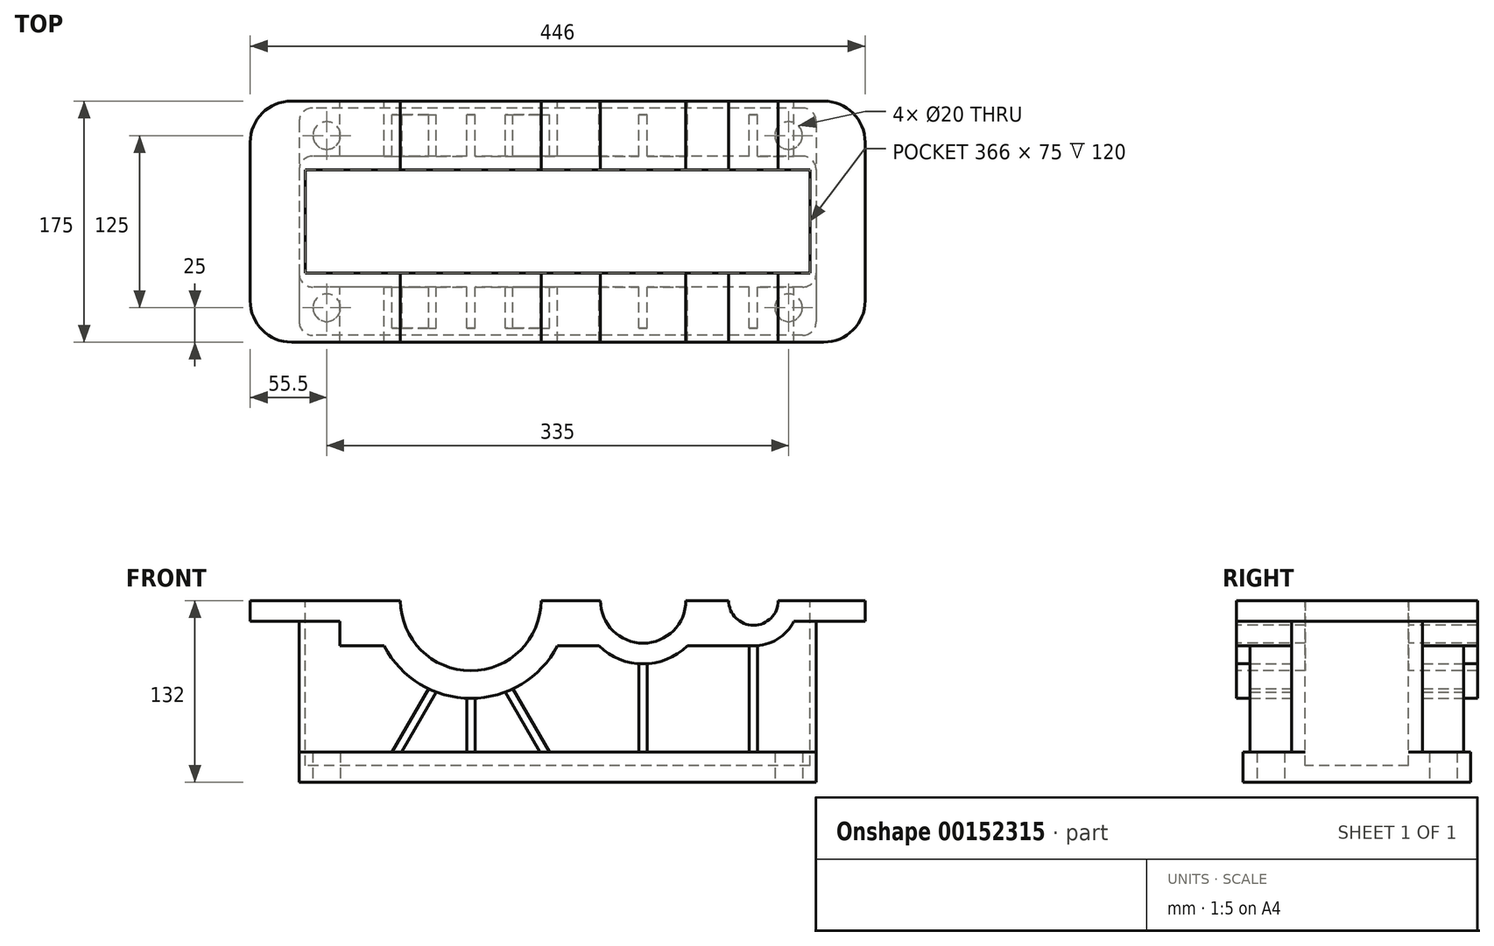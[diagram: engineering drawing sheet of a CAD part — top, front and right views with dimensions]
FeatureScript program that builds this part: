
annotation { "Feature Type Name" : "Feature", "Feature Type Description" : "" }
export const myFeature = defineFeature(function(context is Context, id is Id, definition is map)
    precondition{}
    {
        {
            var Q0;
            Q0=qCreatedBy(makeId("Top.planeOp"),FACE);
            var sketch = newSketch(context, id + "F0", { "sketchPlane" : qUnion([Q0])});
            skLineSegment(sketch, "E0.bottom", {"start": v(187.5, 82.5) * mm, "end": v(-187.5, 82.5) * mm});
            skLineSegment(sketch, "E0.top", {"start": v(187.5, -82.5) * mm, "end": v(-187.5, -82.5) * mm});
            skLineSegment(sketch, "E0.left", {"start": v(187.5, 82.5) * mm, "end": v(187.5, -82.5) * mm});
            skLineSegment(sketch, "E0.right", {"start": v(-187.5, 82.5) * mm, "end": v(-187.5, -82.5) * mm});
            skPoint(sketch, "E0.middle", {"position": v(0, 0) * mm});
            skSolve(sketch);
        }
        {
            var Q0;
            Q0 = qSketchRegion(id + "F0", true);
            extrude(context, id + "F1", {"entities" : qUnion([Q0]), "depth" : 22 * mm});
        }
        {
            var Q0;
            Q0=makeQuery(id+"F1.opExtrude","CAP_FACE",FACE,{"disambiguationData":[OSD([sQuery(id+"F0.wireOp",EDGE,"E0.bottom"),sQuery(id+"F0.wireOp",EDGE,"E0.top"),sQuery(id+"F0.wireOp",EDGE,"E0.left"),sQuery(id+"F0.wireOp",EDGE,"E0.right")])],"isStart":false});
            var sketch = newSketch(context, id + "F2", { "sketchPlane" : qUnion([Q0])});
            skLineSegment(sketch, "E1.bottom", {"start": v(187.5, 47.5) * mm, "end": v(-187.5, 47.5) * mm});
            skLineSegment(sketch, "E1.top", {"start": v(187.5, -47.5) * mm, "end": v(-187.5, -47.5) * mm});
            skLineSegment(sketch, "E1.left", {"start": v(187.5, 47.5) * mm, "end": v(187.5, -47.5) * mm});
            skLineSegment(sketch, "E1.right", {"start": v(-187.5, 47.5) * mm, "end": v(-187.5, -47.5) * mm});
            skPoint(sketch, "E1.middle", {"position": v(0, 0) * mm});
            skSolve(sketch);
        }
        {
            var Q0;
            Q0 = qSketchRegion(id + "F2", true);
            extrude(context, id + "F3", {"entities" : qUnion([Q0]), "operationType" : NewBodyOperationType.ADD, "depth" : 95 * mm});
        }
        {
            var Q0;
            Q0=makeQuery(id+"F1.opExtrude","SWEPT_EDGE",EDGE,{"disambiguationData":[OSD([sQuery(id+"F0.wireOp",EDGE,"E0.top"),sQuery(id+"F0.wireOp",EDGE,"E0.right")])]});
            var Q1;
            Q1=makeQuery(id+"F1.opExtrude","SWEPT_EDGE",EDGE,{"disambiguationData":[OSD([sQuery(id+"F0.wireOp",EDGE,"E0.top"),sQuery(id+"F0.wireOp",EDGE,"E0.left")])]});
            var Q2;
            Q2=makeQuery(id+"F1.opExtrude","SWEPT_EDGE",EDGE,{"disambiguationData":[OSD([sQuery(id+"F0.wireOp",EDGE,"E0.bottom"),sQuery(id+"F0.wireOp",EDGE,"E0.left")])]});
            var Q3;
            Q3=makeQuery(id+"F3.opExtrude","SWEPT_EDGE",EDGE,{"disambiguationData":[OSD([sQuery(id+"F0.wireOp",EDGE,"E0.left"),sQuery(id+"F2.wireOp",EDGE,"E1.bottom"),sQuery(id+"F2.wireOp",EDGE,"E1.left")])]});
            var Q4;
            Q4=makeQuery(id+"F3.opExtrude","SWEPT_EDGE",EDGE,{"disambiguationData":[OSD([sQuery(id+"F0.wireOp",EDGE,"E0.left"),sQuery(id+"F2.wireOp",EDGE,"E1.top"),sQuery(id+"F2.wireOp",EDGE,"E1.left")])]});
            var Q5;
            Q5=makeQuery(id+"F3.opExtrude","SWEPT_EDGE",EDGE,{"disambiguationData":[OSD([sQuery(id+"F0.wireOp",EDGE,"E0.right"),sQuery(id+"F2.wireOp",EDGE,"E1.top"),sQuery(id+"F2.wireOp",EDGE,"E1.right")])]});
            var Q6;
            Q6=makeQuery(id+"F3.opExtrude","SWEPT_EDGE",EDGE,{"disambiguationData":[OSD([sQuery(id+"F0.wireOp",EDGE,"E0.right"),sQuery(id+"F2.wireOp",EDGE,"E1.bottom"),sQuery(id+"F2.wireOp",EDGE,"E1.right")])]});
            var Q7;
            Q7=makeQuery(id+"F1.opExtrude","SWEPT_EDGE",EDGE,{"disambiguationData":[OSD([sQuery(id+"F0.wireOp",EDGE,"E0.bottom"),sQuery(id+"F0.wireOp",EDGE,"E0.right")])]});
            fillet(context, id + "F4", {"entities" : qUnion([Q0, Q1, Q2, Q3, Q4, Q5, Q6, Q7]), "radius" : 10 * mm, "tangentPropagation" : true, "allowEdgeOverflow" : false});
        }
        {
            var Q0;
            Q0=qCreatedBy(makeId("Front.planeOp"),FACE);
            var sketch = newSketch(context, id + "F5", { "sketchPlane" : qUnion([Q0])});
            skLineSegment(sketch, "E2", {"start": v(-223, 132) * mm, "end": v(223, 132) * mm});
            skLineSegment(sketch, "E3", {"start": v(223, 132) * mm, "end": v(223, 117) * mm});
            skLineSegment(sketch, "E4", {"start": v(223, 117) * mm, "end": v(171.4, 117) * mm});
            skLineSegment(sketch, "E5", {"start": v(-223, 132) * mm, "end": v(-223, 117) * mm});
            skLineSegment(sketch, "E6", {"start": v(-223, 117) * mm, "end": v(-157.86, 117) * mm});
            skLineSegment(sketch, "E7", {"start": v(-157.86, 117) * mm, "end": v(-157.86, 99) * mm});
            skLineSegment(sketch, "E8", {"start": v(-157.86, 99) * mm, "end": v(-125.86, 99) * mm});
            skLineSegment(sketch, "E9", {"start": v(0, 132) * mm, "end": v(0, 0) * mm, "construction": true});
            skLineSegment(sketch, "E10", {"start": v(-63, 132) * mm, "end": v(-63, 21.3) * mm, "construction": true});
            skLineSegment(sketch, "E11", {"start": v(62, 132) * mm, "end": v(62, 21.78) * mm, "construction": true});
            skLineSegment(sketch, "E12", {"start": v(142, 132) * mm, "end": v(142, 22.17) * mm, "construction": true});
            skArc(sketch, "E13", {"start": v(-125.86, 99) * mm, "mid": v(-63, 61) * mm, "end": v(-0.14, 99) * mm});
            skLineSegment(sketch, "E14", {"start": v(-0.14, 99) * mm, "end": v(29.95, 99) * mm});
            skArc(sketch, "E15", {"start": v(29.95, 99) * mm, "mid": v(62, 86) * mm, "end": v(94.05, 99) * mm});
            skLineSegment(sketch, "E16", {"start": v(94.05, 99) * mm, "end": v(142, 99) * mm});
            skArc(sketch, "E17", {"start": v(142, 99) * mm, "mid": v(159.23, 103.86) * mm, "end": v(171.4, 117) * mm});
            skSolve(sketch);
        }
        {
            var Q0;
            Q0 = qSketchRegion(id + "F5", true);
            extrude(context, id + "F6", {"entities" : qUnion([Q0]), "operationType" : NewBodyOperationType.ADD, "endBound" : BoundingType.SYMMETRIC, "depth" : 175 * mm});
        }
        {
            var Q0;
            Q0=qCreatedBy(makeId("Front.planeOp"),FACE);
            var sketch = newSketch(context, id + "F7", { "sketchPlane" : qUnion([Q0])});
            skLineSegment(sketch, "E18.0", {"start": v(-63, 132) * mm, "end": v(-63, 21.3) * mm, "construction": true});
            skLineSegment(sketch, "E19.0", {"start": v(62, 132) * mm, "end": v(62, 21.78) * mm, "construction": true});
            skLineSegment(sketch, "E20.0", {"start": v(142, 132) * mm, "end": v(142, 22.17) * mm, "construction": true});
            skLineSegment(sketch, "E21.bottom", {"start": v(-60, 132) * mm, "end": v(-66, 132) * mm});
            skLineSegment(sketch, "E21.top", {"start": v(-60, 22) * mm, "end": v(-66, 22) * mm});
            skLineSegment(sketch, "E21.left", {"start": v(-60, 132) * mm, "end": v(-60, 22) * mm});
            skLineSegment(sketch, "E21.right", {"start": v(-66, 132) * mm, "end": v(-66, 22) * mm});
            skPoint(sketch, "E21.middle", {"position": v(-63, 77) * mm});
            skLineSegment(sketch, "E22.bottom", {"start": v(65, 132) * mm, "end": v(59, 132) * mm});
            skLineSegment(sketch, "E22.top", {"start": v(65, 22) * mm, "end": v(59, 22) * mm});
            skLineSegment(sketch, "E22.left", {"start": v(65, 132) * mm, "end": v(65, 22) * mm});
            skLineSegment(sketch, "E22.right", {"start": v(59, 132) * mm, "end": v(59, 22) * mm});
            skPoint(sketch, "E22.middle", {"position": v(62, 77) * mm});
            skLineSegment(sketch, "E23.bottom", {"start": v(145, 132) * mm, "end": v(139, 132) * mm});
            skLineSegment(sketch, "E23.top", {"start": v(145, 22) * mm, "end": v(139, 22) * mm});
            skLineSegment(sketch, "E23.left", {"start": v(145, 132) * mm, "end": v(145, 22) * mm});
            skLineSegment(sketch, "E23.right", {"start": v(139, 132) * mm, "end": v(139, 22) * mm});
            skPoint(sketch, "E23.middle", {"position": v(142, 77) * mm});
            skLineSegment(sketch, "E24", {"start": v(-11.2, 19) * mm, "end": v(-44.73, 77.08) * mm});
            skLineSegment(sketch, "E25", {"start": v(-44.73, 77.08) * mm, "end": v(-39.53, 80.08) * mm});
            skLineSegment(sketch, "E26", {"start": v(-39.53, 80.08) * mm, "end": v(-6, 22) * mm});
            skLineSegment(sketch, "E27", {"start": v(-6, 22) * mm, "end": v(-11.2, 19) * mm});
            skLineSegment(sketch, "E28.MirrorCS", {"start": v(-120, 22) * mm, "end": v(-114.8, 19) * mm});
            skLineSegment(sketch, "E29.MirrorCS", {"start": v(-81.27, 77.08) * mm, "end": v(-86.47, 80.08) * mm});
            skLineSegment(sketch, "E30.MirrorCS", {"start": v(-114.8, 19) * mm, "end": v(-81.27, 77.08) * mm});
            skLineSegment(sketch, "E31.MirrorCS", {"start": v(-86.47, 80.08) * mm, "end": v(-120, 22) * mm});
            skSolve(sketch);
        }
        {
            var Q0;
            Q0 = qSketchRegion(id + "F7", true);
            extrude(context, id + "F8", {"entities" : qUnion([Q0]), "operationType" : NewBodyOperationType.ADD, "endBound" : BoundingType.SYMMETRIC, "depth" : 155 * mm});
        }
        {
            var Q0;
            Q0=makeQuery(id+"F6.opExtrude","CAP_EDGE",EDGE,{"disambiguationData":[OSD([sQuery(id+"F5.wireOp",EDGE,"E3")])],"isStart":false});
            var Q1;
            Q1=makeQuery(id+"F6.opExtrude","CAP_EDGE",EDGE,{"disambiguationData":[OSD([sQuery(id+"F5.wireOp",EDGE,"E3")])],"isStart":true});
            var Q2;
            Q2=makeQuery(id+"F6.opExtrude","CAP_EDGE",EDGE,{"disambiguationData":[OSD([sQuery(id+"F5.wireOp",EDGE,"E5")])],"isStart":true});
            var Q3;
            Q3=makeQuery(id+"F6.opExtrude","CAP_EDGE",EDGE,{"disambiguationData":[OSD([sQuery(id+"F5.wireOp",EDGE,"E5")])],"isStart":false});
            fillet(context, id + "F9", {"entities" : qUnion([Q0, Q1, Q2, Q3]), "radius" : 30 * mm, "tangentPropagation" : true, "allowEdgeOverflow" : false});
        }
        {
            var Q0;
            Q0=qCreatedBy(makeId("Front.planeOp"),FACE);
            var sketch = newSketch(context, id + "F10", { "sketchPlane" : qUnion([Q0])});
            skPoint(sketch, "E32.0", {"position": v(-63, 132) * mm});
            skPoint(sketch, "E33.0", {"position": v(62, 132) * mm});
            skPoint(sketch, "E34.0", {"position": v(142, 132) * mm});
            skCircle(sketch, "E35", {"center": v(-63, 132) * mm, "radius": 51 * mm});
            skCircle(sketch, "E36", {"center": v(62, 132) * mm, "radius": 31 * mm});
            skCircle(sketch, "E37", {"center": v(142, 132) * mm, "radius": 18 * mm});
            skSolve(sketch);
        }
        {
            var Q0;
            Q0 = qSketchRegion(id + "F10", true);
            extrude(context, id + "F11", {"entities" : qUnion([Q0]), "operationType" : NewBodyOperationType.REMOVE, "endBound" : BoundingType.THROUGH_ALL, "oppositeDirection" : true, "depth" : 25 * mm, "hasSecondDirection" : true, "secondDirectionBound" : SecondDirectionBoundingType.THROUGH_ALL, "secondDirectionOppositeDirection" : false, "secondDirectionDepth" : 25 * mm});
        }
        {
            var Q0;
            {var subQ0=sQuery(id+"F5.wireOp",EDGE,"E17");var subQ1=sQuery(id+"F5.wireOp",EDGE,"E16");var subQ2=sQuery(id+"F5.wireOp",EDGE,"E15");var subQ3=sQuery(id+"F5.wireOp",EDGE,"E14");var subQ4=sQuery(id+"F5.wireOp",EDGE,"E13");var subQ5=sQuery(id+"F5.wireOp",EDGE,"E8");var subQ6=sQuery(id+"F5.wireOp",EDGE,"E7");var subQ7=sQuery(id+"F5.wireOp",EDGE,"E6");var subQ8=sQuery(id+"F5.wireOp",EDGE,"E5");var subQ9=sQuery(id+"F5.wireOp",EDGE,"E4");var subQ10=sQuery(id+"F5.wireOp",EDGE,"E3");var subQ11=sQuery(id+"F5.wireOp",EDGE,"E2");Q0=makeQuery(id+"F11.boolean.opBoolean","SPLIT",FACE,{"disambiguationData":[TD([makeQuery(id+"F6.opExtrude","CAP_FACE",FACE,{"disambiguationData":[OSD([subQ11,subQ10,subQ9,subQ8,subQ7,subQ6,subQ5,subQ4,subQ3,subQ2,subQ1,subQ0])],"isStart":true}),makeQuery(id+"F6.opExtrude","CAP_FACE",FACE,{"disambiguationData":[OSD([subQ11,subQ10,subQ9,subQ8,subQ7,subQ6,subQ5,subQ4,subQ3,subQ2,subQ1,subQ0])],"isStart":false}),makeQuery(id+"F6.opExtrude","SWEPT_FACE",FACE,{"disambiguationData":[OSD([subQ8])]}),makeQuery(id+"F9.opFillet","BLEND_FACE",FACE,{"disambiguationData":[OSD([subQ8]),TDD([makeQuery(id+"F6.opExtrude","CAP_EDGE",EDGE,{"disambiguationData":[OSD([subQ8])],"isStart":true})])]}),makeQuery(id+"F9.opFillet","BLEND_FACE",FACE,{"disambiguationData":[OSD([subQ8]),TDD([makeQuery(id+"F6.opExtrude","CAP_EDGE",EDGE,{"disambiguationData":[OSD([subQ8])],"isStart":false})])]}),makeQuery(id+"F11.opExtrude","SWEPT_FACE",FACE,{"disambiguationData":[OSD([sQuery(id+"F10.wireOp",EDGE,"E35")])]})])],"derivedFrom":makeQuery(id+"F6.opExtrude","SWEPT_FACE",FACE,{"disambiguationData":[OSD([subQ11])]})});}
            var sketch = newSketch(context, id + "F12", { "sketchPlane" : qUnion([Q0])});
            skLineSegment(sketch, "E38.bottom", {"start": v(183, 37.5) * mm, "end": v(-183, 37.5) * mm});
            skLineSegment(sketch, "E38.top", {"start": v(183, -37.5) * mm, "end": v(-183, -37.5) * mm});
            skLineSegment(sketch, "E38.left", {"start": v(183, 37.5) * mm, "end": v(183, -37.5) * mm});
            skLineSegment(sketch, "E38.right", {"start": v(-183, 37.5) * mm, "end": v(-183, -37.5) * mm});
            skPoint(sketch, "E38.middle", {"position": v(0, 0) * mm});
            skSolve(sketch);
        }
        {
            var Q0;
            Q0 = qSketchRegion(id + "F12", true);
            extrude(context, id + "F13", {"entities" : qUnion([Q0]), "operationType" : NewBodyOperationType.REMOVE, "oppositeDirection" : true, "depth" : 120 * mm});
        }
        {
            var Q0;
            Q0=makeQuery(id+"F1.opExtrude","CAP_FACE",FACE,{"disambiguationData":[OSD([sQuery(id+"F0.wireOp",EDGE,"E0.bottom"),sQuery(id+"F0.wireOp",EDGE,"E0.top"),sQuery(id+"F0.wireOp",EDGE,"E0.left"),sQuery(id+"F0.wireOp",EDGE,"E0.right")])],"isStart":true});
            var sketch = newSketch(context, id + "F14", { "sketchPlane" : qUnion([Q0])});
            skLineSegment(sketch, "E39.bottom", {"start": v(167.5, 62.5) * mm, "end": v(-167.5, 62.5) * mm, "construction": true});
            skLineSegment(sketch, "E39.top", {"start": v(167.5, -62.5) * mm, "end": v(-167.5, -62.5) * mm, "construction": true});
            skLineSegment(sketch, "E39.left", {"start": v(167.5, 62.5) * mm, "end": v(167.5, -62.5) * mm, "construction": true});
            skLineSegment(sketch, "E39.right", {"start": v(-167.5, 62.5) * mm, "end": v(-167.5, -62.5) * mm, "construction": true});
            skPoint(sketch, "E39.middle", {"position": v(0, 0) * mm});
            skCircle(sketch, "E40", {"center": v(-167.5, 62.5) * mm, "radius": 10 * mm});
            skCircle(sketch, "E41", {"center": v(-167.5, -62.5) * mm, "radius": 10 * mm});
            skCircle(sketch, "E42", {"center": v(167.5, -62.5) * mm, "radius": 10 * mm});
            skCircle(sketch, "E43", {"center": v(167.5, 62.5) * mm, "radius": 10 * mm});
            skSolve(sketch);
        }
        {
            var Q0;
            Q0 = qSketchRegion(id + "F14", true);
            extrude(context, id + "F15", {"entities" : qUnion([Q0]), "operationType" : NewBodyOperationType.REMOVE, "oppositeDirection" : true, "depth" : 25 * mm});
        }
    });
